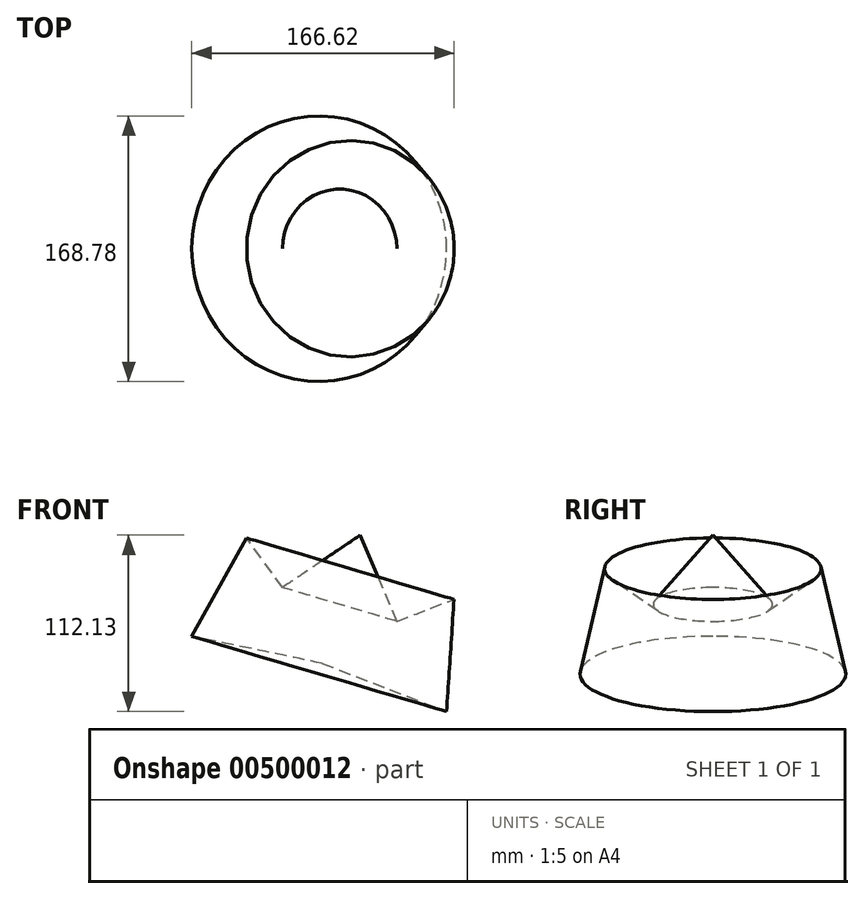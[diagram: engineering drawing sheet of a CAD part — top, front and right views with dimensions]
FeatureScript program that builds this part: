
annotation { "Feature Type Name" : "Feature", "Feature Type Description" : "" }
export const myFeature = defineFeature(function(context is Context, id is Id, definition is map)
    precondition{}
    {
        {
            var Q0;
            Q0=qCreatedBy(makeId("Front.planeOp"),FACE);
            var sketch = newSketch(context, id + "F0", { "sketchPlane" : qUnion([Q0])});
            skLineSegment(sketch, "E0", {"start": v(-22.66, 45.18) * mm, "end": v(-57.66, -17.64) * mm});
            skLineSegment(sketch, "E1", {"start": v(-22.95, 44.9) * mm, "end": v(0, 13.34) * mm});
            skLineSegment(sketch, "E2", {"start": v(0, 13.34) * mm, "end": v(49.34, 46.62) * mm});
            skLineSegment(sketch, "E3", {"start": v(49.34, 46.62) * mm, "end": v(25.25, -34.86) * mm});
            skLineSegment(sketch, "E4", {"start": v(25.25, -34.86) * mm, "end": v(-57.66, -17.64) * mm});
            skSolve(sketch);
        }
        {
            var Q0;
            {var subQ0=sQuery(id+"F0.wireOp",EDGE,"E2");Q0=makeQuery(id+"F0.imprint","IMPRINT",FACE,{"disambiguationData":[TD([[makeQuery(id+"F0.imprint","IMPRINT",EDGE,{"derivedFrom":subQ0}),-1.0]])]});}
            var Q1;
            Q1=sQuery(id+"F0.wireOp",EDGE,"E3");
            revolve(context, id + "F1", {"entities" : qUnion([Q0]), "axis" : qUnion([Q1]), "revolveType" : RevolveType.FULL});
        }
    });
